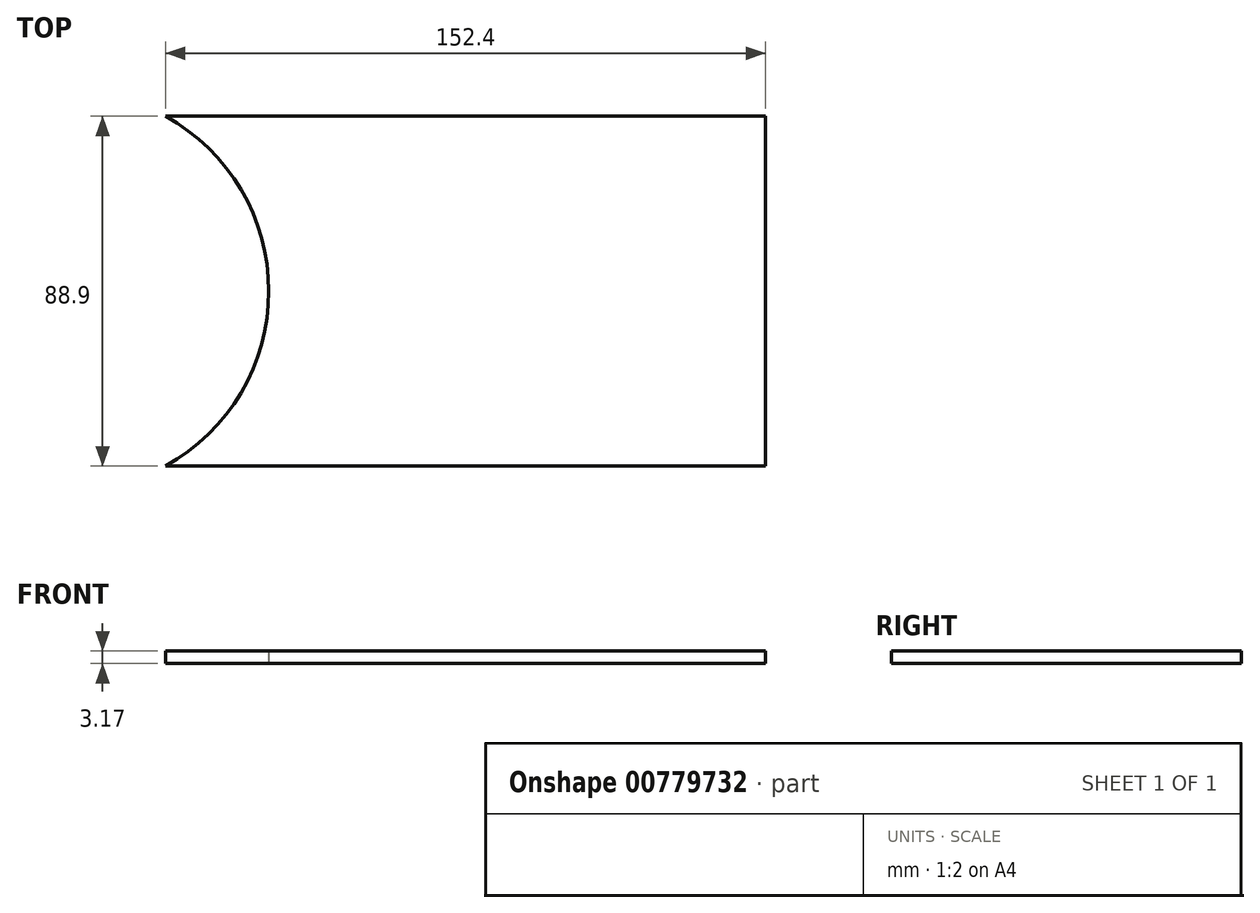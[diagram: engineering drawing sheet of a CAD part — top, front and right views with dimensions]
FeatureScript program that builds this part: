
annotation { "Feature Type Name" : "Feature", "Feature Type Description" : "" }
export const myFeature = defineFeature(function(context is Context, id is Id, definition is map)
    precondition{}
    {
        {
            var Q0;
            Q0=qCreatedBy(makeId("Top.planeOp"),FACE);
            var sketch = newSketch(context, id + "F0", { "sketchPlane" : qUnion([Q0])});
            skLineSegment(sketch, "E0.bottom", {"start": v(-76.2, 44.45) * mm, "end": v(76.2, 44.45) * mm});
            skLineSegment(sketch, "E0.top", {"start": v(-76.2, -44.45) * mm, "end": v(76.2, -44.45) * mm});
            skLineSegment(sketch, "E0.right", {"start": v(76.2, 44.45) * mm, "end": v(76.2, -44.45) * mm});
            skPoint(sketch, "E0.middle", {"position": v(0, 0) * mm});
            skArc(sketch, "E1", {"start": v(-76.2, -44.45) * mm, "mid": v(-50, 0) * mm, "end": v(-76.2, 44.45) * mm});
            skSolve(sketch);
        }
        {
            var Q0;
            Q0=makeQuery(id+"F0.imprint","IMPRINT",FACE,{"disambiguationData":[TD([[makeQuery(id+"F0.imprint","IMPRINT",EDGE,{"derivedFrom":sQuery(id+"F0.wireOp",EDGE,"E0.bottom")}),-1.0]])]});
            extrude(context, id + "F1", {"entities" : qUnion([Q0]), "depth" : 3.17 * mm, "offsetDistance" : 25.4 * mm});
        }
    });
